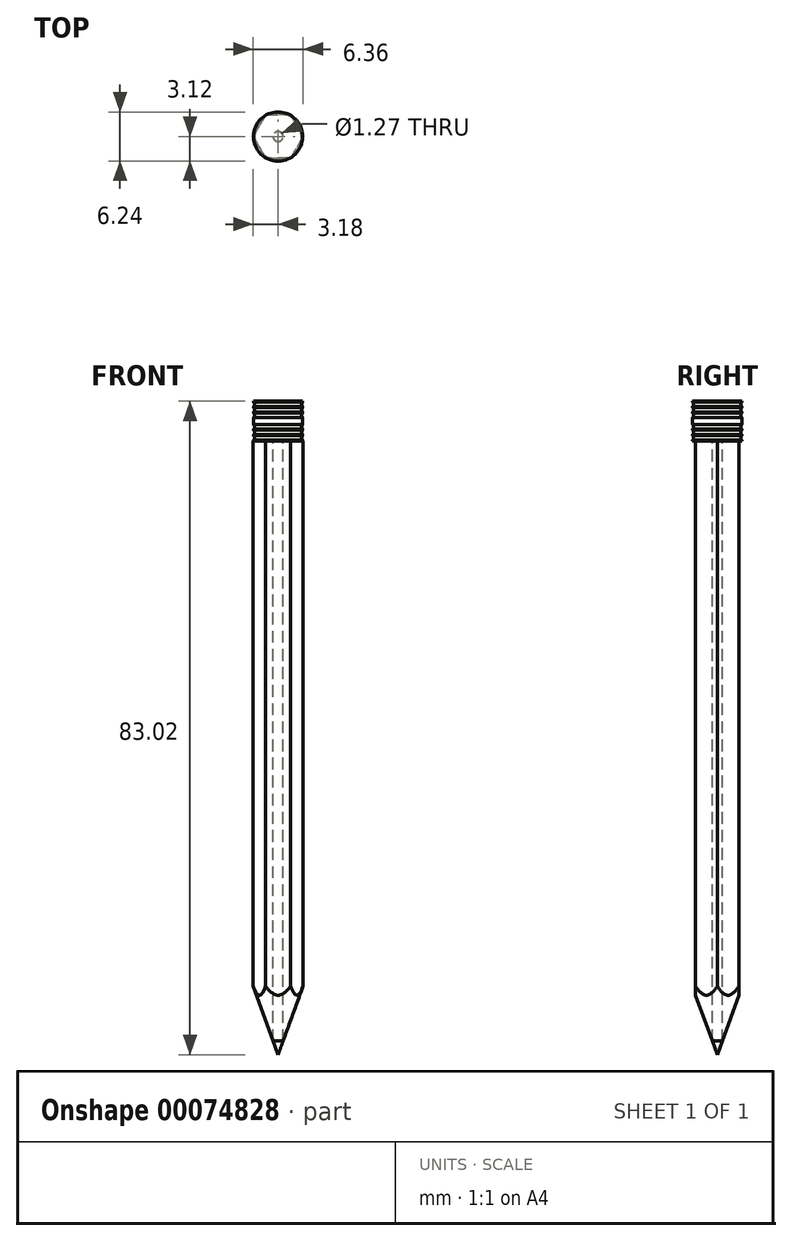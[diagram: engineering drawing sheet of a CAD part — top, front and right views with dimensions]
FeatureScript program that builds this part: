
annotation { "Feature Type Name" : "Feature", "Feature Type Description" : "" }
export const myFeature = defineFeature(function(context is Context, id is Id, definition is map)
    precondition{}
    {
        {
            var Q0;
            Q0=qCreatedBy(makeId("Top.planeOp"),FACE);
            var sketch = newSketch(context, id + "F0", { "sketchPlane" : qUnion([Q0])});
            skCircle(sketch, "E0.cCircle", {"center": v(0, 0) * mm, "radius": 3.18 * mm, "construction": true});
            skLineSegment(sketch, "E0.0", {"start": v(-3.18, 0) * mm, "end": v(-1.59, 2.75) * mm});
            skLineSegment(sketch, "E0.1", {"start": v(-1.59, 2.75) * mm, "end": v(1.59, 2.75) * mm});
            skLineSegment(sketch, "E0.2", {"start": v(1.59, 2.75) * mm, "end": v(3.18, 0) * mm});
            skLineSegment(sketch, "E0.3", {"start": v(3.18, 0) * mm, "end": v(1.59, -2.75) * mm});
            skLineSegment(sketch, "E0.4", {"start": v(1.59, -2.75) * mm, "end": v(-1.59, -2.75) * mm});
            skLineSegment(sketch, "E0.5", {"start": v(-1.59, -2.75) * mm, "end": v(-3.18, 0) * mm});
            skSolve(sketch);
        }
        {
            var Q0;
            Q0 = qSketchRegion(id + "F0", true);
            extrude(context, id + "F1", {"entities" : qUnion([Q0]), "depth" : 76.2 * mm});
        }
        {
            var Q0;
            Q0=qCreatedBy(makeId("Top.planeOp"),FACE);
            var sketch = newSketch(context, id + "F2", { "sketchPlane" : qUnion([Q0])});
            skCircle(sketch, "E1", {"center": v(0, 0) * mm, "radius": 0.64 * mm});
            skSolve(sketch);
        }
        {
            var Q0;
            Q0 = qSketchRegion(id + "F2", true);
            extrude(context, id + "F3", {"entities" : qUnion([Q0]), "operationType" : NewBodyOperationType.REMOVE, "endBound" : BoundingType.THROUGH_ALL, "depth" : 25.4 * mm});
        }
        {
            var Q0;
            Q0=qCreatedBy(makeId("Right.planeOp"),FACE);
            var sketch = newSketch(context, id + "F4", { "sketchPlane" : qUnion([Q0])});
            skLineSegment(sketch, "E2", {"start": v(-0.64, 0) * mm, "end": v(-0.64, 12.7) * mm, "construction": true});
            skLineSegment(sketch, "E3", {"start": v(-0.64, 12.7) * mm, "end": v(-5.26, 12.7) * mm, "construction": true});
            skLineSegment(sketch, "E4", {"start": v(-5.26, 12.7) * mm, "end": v(-0.64, 0) * mm});
            skLineSegment(sketch, "E5", {"start": v(-5.26, 12.7) * mm, "end": v(-5.26, 0) * mm});
            skLineSegment(sketch, "E6", {"start": v(-5.26, 0) * mm, "end": v(-0.64, 0) * mm});
            skLineSegment(sketch, "E7", {"start": v(0, 0) * mm, "end": v(0, 12.7) * mm, "construction": true});
            skSolve(sketch);
        }
        {
            var Q0;
            Q0 = qSketchRegion(id + "F4", true);
            var Q1;
            Q1=sQuery(id+"F4.wireOp",EDGE,"E7");
            revolve(context, id + "F5", {"operationType" : NewBodyOperationType.REMOVE, "entities" : qUnion([Q0]), "axis" : qUnion([Q1]), "revolveType" : RevolveType.FULL, "oppositeDirection" : true});
        }
        {
            var Q0;
            Q0=makeQuery(id+"F1.opExtrude","CAP_FACE",FACE,{"disambiguationData":[OSD([sQuery(id+"F0.wireOp",EDGE,"E0.0"),sQuery(id+"F0.wireOp",EDGE,"E0.1"),sQuery(id+"F0.wireOp",EDGE,"E0.2"),sQuery(id+"F0.wireOp",EDGE,"E0.3"),sQuery(id+"F0.wireOp",EDGE,"E0.4"),sQuery(id+"F0.wireOp",EDGE,"E0.5")])],"isStart":false});
            var sketch = newSketch(context, id + "F6", { "sketchPlane" : qUnion([Q0])});
            skCircle(sketch, "E8", {"center": v(0, 0) * mm, "radius": 0.64 * mm});
            skSolve(sketch);
        }
        {
            var Q0;
            Q0 = qSketchRegion(id + "F6", true);
            extrude(context, id + "F7", {"entities" : qUnion([Q0]), "oppositeDirection" : true, "depth" : 129.54 * mm});
        }
        {
            var Q0;
            Q0=qCreatedBy(makeId("Right.planeOp"),FACE);
            var sketch = newSketch(context, id + "F8", { "sketchPlane" : qUnion([Q0])});
            skLineSegment(sketch, "E9.0", {"start": v(-5.26, 12.7) * mm, "end": v(-0.63, 0) * mm, "construction": true});
            skLineSegment(sketch, "E10.0", {"start": v(0, 0) * mm, "end": v(0, 12.7) * mm, "construction": true});
            skLineSegment(sketch, "E11", {"start": v(-0.63, 0) * mm, "end": v(0, -1.74) * mm});
            skLineSegment(sketch, "E12", {"start": v(-0.63, -53.34) * mm, "end": v(-0.63, 0) * mm});
            skLineSegment(sketch, "E13", {"start": v(0, 0) * mm, "end": v(0, -53.34) * mm, "construction": true});
            skLineSegment(sketch, "E14", {"start": v(-0.63, -53.34) * mm, "end": v(0, -53.34) * mm});
            skLineSegment(sketch, "E15", {"start": v(0, -1.74) * mm, "end": v(0, -53.34) * mm});
            skSolve(sketch);
        }
        {
            var Q0;
            Q0 = qSketchRegion(id + "F8", true);
            var Q1;
            Q1=sQuery(id+"F8.wireOp",EDGE,"E13");
            revolve(context, id + "F9", {"operationType" : NewBodyOperationType.REMOVE, "entities" : qUnion([Q0]), "axis" : qUnion([Q1]), "revolveType" : RevolveType.FULL, "oppositeDirection" : true});
        }
        {
            var Q0;
            Q0=qCreatedBy(makeId("Front.planeOp"),FACE);
            var sketch = newSketch(context, id + "F10", { "sketchPlane" : qUnion([Q0])});
            skLineSegment(sketch, "E16", {"start": v(0, 76.2) * mm, "end": v(0, 135.14) * mm, "construction": true});
            skLineSegment(sketch, "E17", {"start": v(0, 76.2) * mm, "end": v(3.12, 76.2) * mm});
            skLineSegment(sketch, "E18", {"start": v(3.12, 76.2) * mm, "end": v(3.12, 76.33) * mm});
            skLineSegment(sketch, "E19", {"start": v(3.12, 81.28) * mm, "end": v(0, 81.28) * mm});
            skLineSegment(sketch, "E20", {"start": v(0, 81.28) * mm, "end": v(0, 76.2) * mm});
            skArc(sketch, "E21", {"start": v(3.12, 81.15) * mm, "mid": v(3, 80.87) * mm, "end": v(3.12, 80.59) * mm});
            skArc(sketch, "E22", {"start": v(3.12, 80.46) * mm, "mid": v(3, 80.17) * mm, "end": v(3.12, 79.9) * mm});
            skArc(sketch, "E23", {"start": v(3.12, 79.76) * mm, "mid": v(3, 79.48) * mm, "end": v(3.12, 79.2) * mm});
            skArc(sketch, "E24", {"start": v(3.12, 76.9) * mm, "mid": v(3, 76.61) * mm, "end": v(3.12, 76.33) * mm});
            skArc(sketch, "E25", {"start": v(3.12, 77.59) * mm, "mid": v(3, 77.3) * mm, "end": v(3.12, 77.02) * mm});
            skArc(sketch, "E26", {"start": v(3.12, 78.28) * mm, "mid": v(3, 78) * mm, "end": v(3.12, 77.72) * mm});
            skLineSegment(sketch, "E27.trimOffspring", {"start": v(3.12, 81.15) * mm, "end": v(3.12, 81.28) * mm});
            skLineSegment(sketch, "E28.trimOffspring", {"start": v(3.12, 80.46) * mm, "end": v(3.12, 80.59) * mm});
            skLineSegment(sketch, "E29.trimOffspring", {"start": v(3.12, 79.76) * mm, "end": v(3.12, 79.9) * mm});
            skLineSegment(sketch, "E30.trimOffspring", {"start": v(3.12, 78.28) * mm, "end": v(3.12, 79.2) * mm});
            skLineSegment(sketch, "E31.trimOffspring", {"start": v(3.12, 77.59) * mm, "end": v(3.12, 77.72) * mm});
            skLineSegment(sketch, "E32.trimOffspring", {"start": v(3.12, 76.9) * mm, "end": v(3.12, 77.02) * mm});
            skSolve(sketch);
        }
        {
            var Q0;
            Q0 = qSketchRegion(id + "F10", true);
            var Q1;
            Q1=sQuery(id+"F10.wireOp",EDGE,"E16");
            revolve(context, id + "F11", {"entities" : qUnion([Q0]), "axis" : qUnion([Q1]), "revolveType" : RevolveType.FULL});
        }
    });
